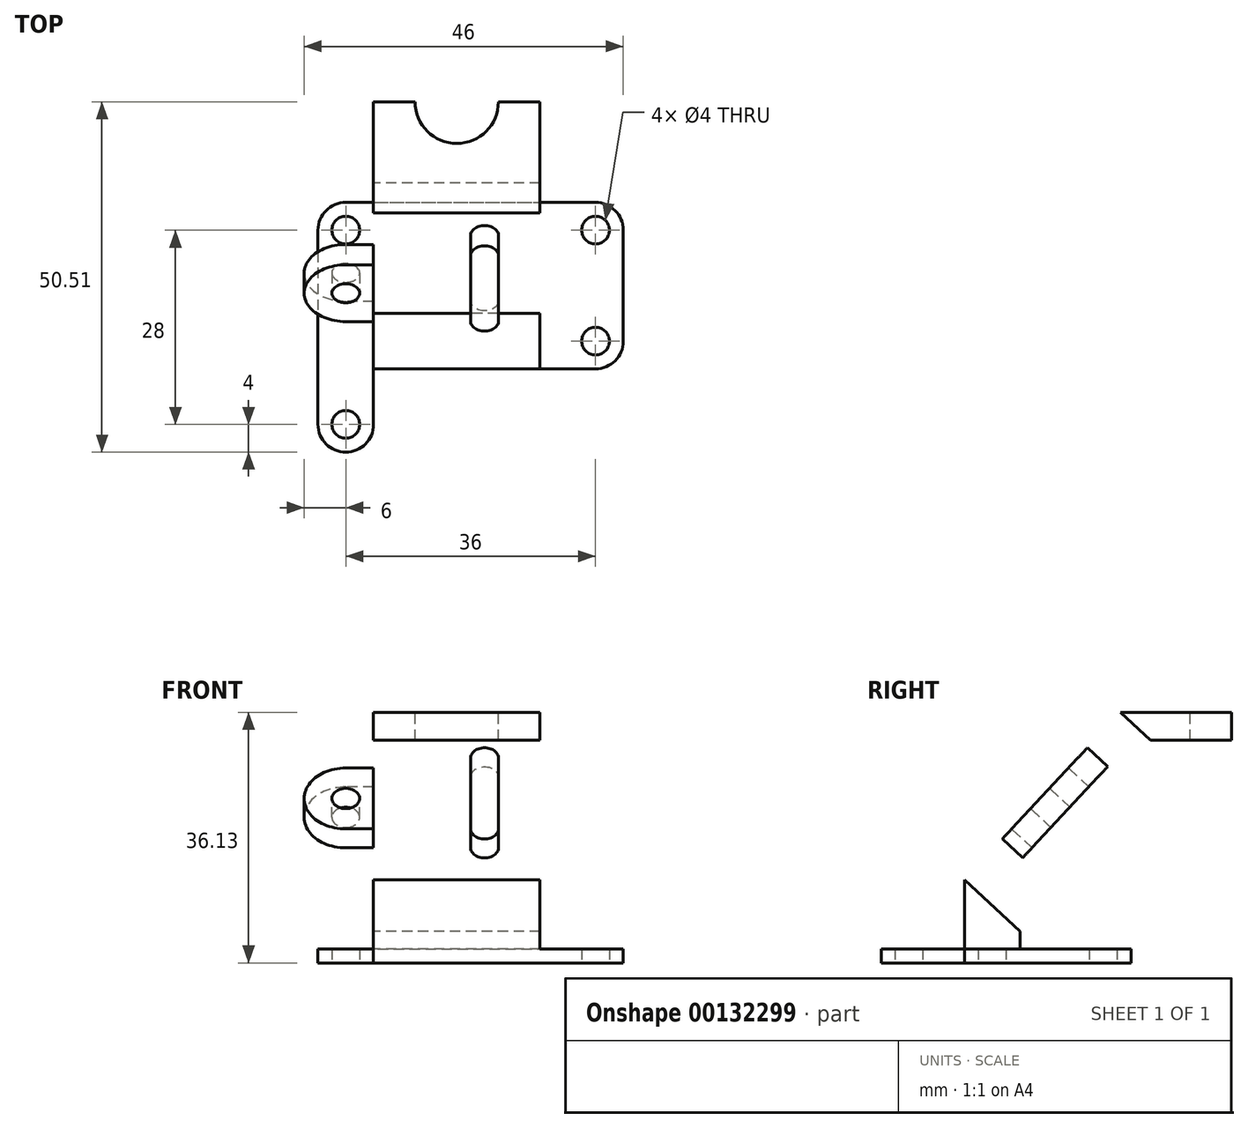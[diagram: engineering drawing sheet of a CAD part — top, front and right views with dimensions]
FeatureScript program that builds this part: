
annotation { "Feature Type Name" : "Feature", "Feature Type Description" : "" }
export const myFeature = defineFeature(function(context is Context, id is Id, definition is map)
    precondition{}
    {
        {
            var Q0;
            Q0=qCreatedBy(makeId("Top.planeOp"),FACE);
            var sketch = newSketch(context, id + "F0", { "sketchPlane" : qUnion([Q0])});
            skLineSegment(sketch, "E0.bottom", {"start": v(0, 0) * mm, "end": v(40, 0) * mm});
            skLineSegment(sketch, "E0.top", {"start": v(4, 24) * mm, "end": v(40, 24) * mm});
            skLineSegment(sketch, "E0.left", {"start": v(0, 0) * mm, "end": v(0, 20) * mm});
            skLineSegment(sketch, "E0.right", {"start": v(44, 4) * mm, "end": v(44, 20) * mm});
            skLineSegment(sketch, "E1", {"start": v(0, 0) * mm, "end": v(0, -8) * mm});
            skLineSegment(sketch, "E2", {"start": v(8, 0) * mm, "end": v(8, -8) * mm});
            skArc(sketch, "E3", {"start": v(0, -8) * mm, "mid": v(4, -12) * mm, "end": v(8, -8) * mm});
            skCircle(sketch, "E4", {"center": v(4, -8) * mm, "radius": 2 * mm});
            skCircle(sketch, "E5", {"center": v(40, 4) * mm, "radius": 2 * mm});
            skLineSegment(sketch, "E6", {"start": v(44, 12) * mm, "end": v(40, 12) * mm, "construction": true});
            skLineSegment(sketch, "E7", {"start": v(22, 24) * mm, "end": v(22, 19.37) * mm, "construction": true});
            skCircle(sketch, "E8.MirrorC", {"center": v(40, 20) * mm, "radius": 2 * mm});
            skCircle(sketch, "E9.MirrorC", {"center": v(4, 20) * mm, "radius": 2 * mm});
            skPoint(sketch, "E10.visualSharp", {"position": v(44, 24) * mm});
            skArc(sketch, "E10.filletArc", {"start": v(44, 20) * mm, "mid": v(42.83, 22.83) * mm, "end": v(40, 24) * mm});
            skPoint(sketch, "E11.visualSharp", {"position": v(44, 0) * mm});
            skArc(sketch, "E11.filletArc", {"start": v(40, 0) * mm, "mid": v(42.83, 1.17) * mm, "end": v(44, 4) * mm});
            skPoint(sketch, "E12.visualSharp", {"position": v(0, 24) * mm});
            skArc(sketch, "E12.filletArc", {"start": v(4, 24) * mm, "mid": v(1.17, 22.83) * mm, "end": v(0, 20) * mm});
            skSolve(sketch);
        }
        {
            var Q0;
            {var subQ1=sQuery(id+"F0.wireOp",EDGE,"E1");Q0=makeQuery(id+"F0.imprint","IMPRINT",FACE,{"disambiguationData":[TD([[makeQuery(id+"F0.imprint","IMPRINT",EDGE,{"derivedFrom":subQ1}),1.0]])]});}
            var Q1;
            Q1=makeQuery(id+"F0.imprint","IMPRINT",FACE,{"disambiguationData":[TD([[makeQuery(id+"F0.imprint","IMPRINT",EDGE,{"derivedFrom":sQuery(id+"F0.wireOp",EDGE,"E0.top")}),-1.0]])]});
            extrude(context, id + "F1", {"entities" : qUnion([Q0, Q1]), "depth" : 2 * mm});
        }
        {
            var Q0;
            Q0=makeQuery(id+"F1.opExtrude","SWEPT_FACE",FACE,{"disambiguationData":[OSD([sQuery(id+"F0.wireOp",EDGE,"E2")])]});
            var sketch = newSketch(context, id + "F2", { "sketchPlane" : qUnion([Q0])});
            skLineSegment(sketch, "E13", {"start": v(0, 2) * mm, "end": v(0, 12) * mm});
            skLineSegment(sketch, "E14", {"start": v(0, 12) * mm, "end": v(22.5, 36.13) * mm});
            skLineSegment(sketch, "E15", {"start": v(22.5, 36.13) * mm, "end": v(38.5, 36.13) * mm});
            skLineSegment(sketch, "E16", {"start": v(38.5, 36.13) * mm, "end": v(38.5, 32.13) * mm});
            skLineSegment(sketch, "E17", {"start": v(38.5, 32.13) * mm, "end": v(24.25, 32.13) * mm});
            skLineSegment(sketch, "E18", {"start": v(24.25, 32.13) * mm, "end": v(8, 14.71) * mm});
            skLineSegment(sketch, "E19", {"start": v(8, 14.71) * mm, "end": v(8, 2) * mm});
            skLineSegment(sketch, "E20", {"start": v(8, 14.71) * mm, "end": v(23.34, 14.71) * mm, "construction": true});
            skLineSegment(sketch, "E21", {"start": v(0, 2) * mm, "end": v(8, 2) * mm});
            skSolve(sketch);
        }
        {
            var Q0;
            Q0=makeQuery(id+"F2.imprint","IMPRINT",FACE,{"disambiguationData":[TD([[makeQuery(id+"F2.imprint","IMPRINT",EDGE,{"derivedFrom":sQuery(id+"F2.wireOp",EDGE,"E13")}),-1.0]])]});
            extrude(context, id + "F3", {"entities" : qUnion([Q0]), "operationType" : NewBodyOperationType.ADD, "depth" : 24 * mm});
        }
        {
            var Q0;
            Q0=makeQuery(id+"F3.opExtrude","SWEPT_FACE",FACE,{"disambiguationData":[OSD([sQuery(id+"F2.wireOp",EDGE,"E14")])]});
            var sketch = newSketch(context, id + "F4", { "sketchPlane" : qUnion([Q0])});
            skLineSegment(sketch, "E22.0.0", {"start": v(8, 41.78) * mm, "end": v(8, 8.78) * mm});
            skLineSegment(sketch, "E22.0.1", {"start": v(8, 8.78) * mm, "end": v(32, 8.78) * mm});
            skLineSegment(sketch, "E22.0.2", {"start": v(32, 8.78) * mm, "end": v(32, 41.78) * mm});
            skLineSegment(sketch, "E22.0.3", {"start": v(32, 41.78) * mm, "end": v(8, 41.78) * mm});
            skLineSegment(sketch, "E23", {"start": v(24, 32.78) * mm, "end": v(24, 18.78) * mm, "construction": true});
            skArc(sketch, "E24.0.startCap", {"start": v(22, 32.78) * mm, "mid": v(24, 34.78) * mm, "end": v(26, 32.78) * mm});
            skArc(sketch, "E24.0.endCap", {"start": v(26, 18.78) * mm, "mid": v(24, 16.78) * mm, "end": v(22, 18.78) * mm});
            skLineSegment(sketch, "E24.0.left", {"start": v(26, 32.78) * mm, "end": v(26, 18.78) * mm});
            skLineSegment(sketch, "E24.0.right", {"start": v(22, 32.78) * mm, "end": v(22, 18.78) * mm});
            skCircle(sketch, "E25", {"center": v(4, 24.78) * mm, "radius": 2 * mm});
            skArc(sketch, "E26", {"start": v(4, 30.78) * mm, "mid": v(-2, 24.78) * mm, "end": v(4, 18.78) * mm});
            skLineSegment(sketch, "E27", {"start": v(8, 30.78) * mm, "end": v(4, 30.78) * mm});
            skLineSegment(sketch, "E28", {"start": v(8, 18.78) * mm, "end": v(4, 18.78) * mm});
            skSolve(sketch);
        }
        {
            var Q0;
            Q0=makeQuery(id+"F4.imprint","IMPRINT",FACE,{"disambiguationData":[TD([[makeQuery(id+"F4.imprint","IMPRINT",EDGE,{"derivedFrom":sQuery(id+"F4.wireOp",EDGE,"E25")}),-1.0]])]});
            extrude(context, id + "F5", {"entities" : qUnion([Q0]), "operationType" : NewBodyOperationType.ADD, "oppositeDirection" : true, "depth" : 4 * mm});
        }
        {
            var Q0;
            Q0=makeQuery(id+"F4.imprint","IMPRINT",FACE,{"disambiguationData":[TD([[makeQuery(id+"F4.imprint","IMPRINT",EDGE,{"derivedFrom":sQuery(id+"F4.wireOp",EDGE,"E24.0.startCap")}),-1.0]])]});
            extrude(context, id + "F6", {"entities" : qUnion([Q0]), "operationType" : NewBodyOperationType.REMOVE, "endBound" : BoundingType.UP_TO_NEXT, "oppositeDirection" : true, "depth" : 10 * mm});
        }
        {
            var Q0;
            Q0=makeQuery(id+"F3.opExtrude","SWEPT_FACE",FACE,{"disambiguationData":[OSD([sQuery(id+"F2.wireOp",EDGE,"E15")])]});
            var sketch = newSketch(context, id + "F7", { "sketchPlane" : qUnion([Q0])});
            skLineSegment(sketch, "E29.0", {"start": v(32, 38.5) * mm, "end": v(8, 38.5) * mm});
            skCircle(sketch, "E30", {"center": v(20, 38.5) * mm, "radius": 6 * mm});
            skSolve(sketch);
        }
        {
            var Q0;
            {var subQ0=sQuery(id+"F7.wireOp",EDGE,"E30");var subQ1=sQuery(id+"F7.wireOp",EDGE,"E29.0");var subQ2=makeQuery(id+"F7.imprint","INTERSECT",VERTEX,{"disambiguationData":[OD(0.0)],"derivedFrom":[subQ1,subQ0]});Q0=makeQuery(id+"F7.imprint","IMPRINT",FACE,{"disambiguationData":[TD([[makeQuery(id+"F7.imprint","IMPRINT",EDGE,{"disambiguationData":[TD([[subQ2,-1.0]])],"derivedFrom":subQ1}),-1.0]])]});}
            var Q1;
            {var subQ0=sQuery(id+"F7.wireOp",EDGE,"E30");var subQ1=sQuery(id+"F7.wireOp",EDGE,"E29.0");var subQ2=makeQuery(id+"F7.imprint","INTERSECT",VERTEX,{"disambiguationData":[OD(0.0)],"derivedFrom":[subQ1,subQ0]});Q1=makeQuery(id+"F7.imprint","IMPRINT",FACE,{"disambiguationData":[TD([[makeQuery(id+"F7.imprint","IMPRINT",EDGE,{"disambiguationData":[TD([[subQ2,-1.0]])],"derivedFrom":subQ1}),1.0]])]});}
            extrude(context, id + "F8", {"entities" : qUnion([Q0, Q1]), "operationType" : NewBodyOperationType.REMOVE, "oppositeDirection" : true, "depth" : 10 * mm});
        }
    });
